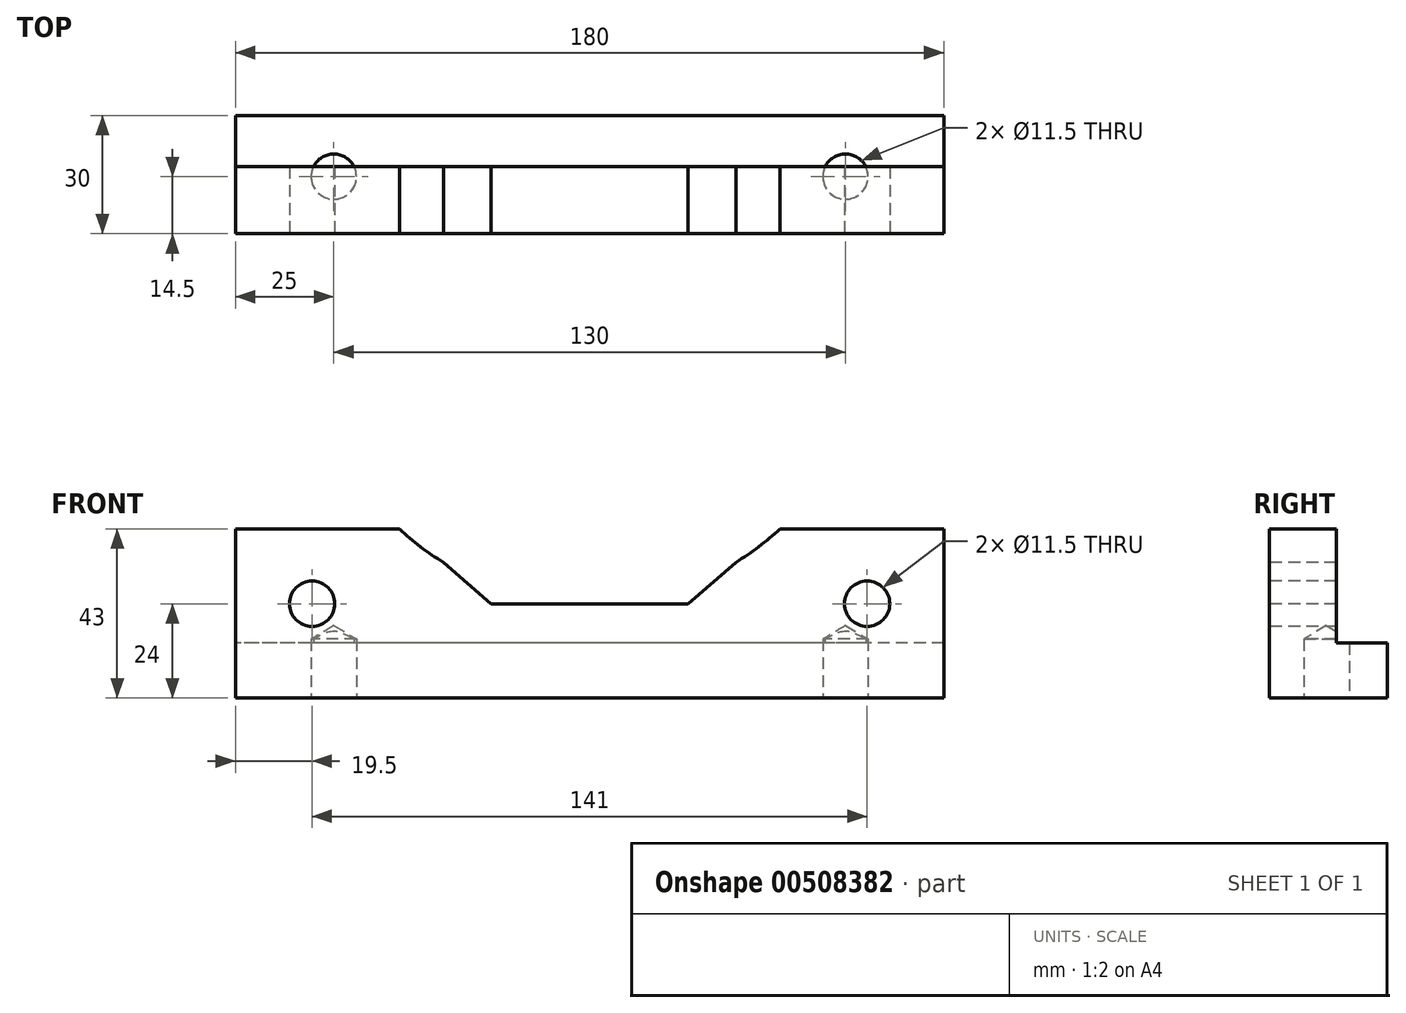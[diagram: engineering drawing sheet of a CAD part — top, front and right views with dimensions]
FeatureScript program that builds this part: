
annotation { "Feature Type Name" : "Feature", "Feature Type Description" : "" }
export const myFeature = defineFeature(function(context is Context, id is Id, definition is map)
    precondition{}
    {
        {
            var Q0;
            Q0=qCreatedBy(makeId("Right.planeOp"),FACE);
            var sketch = newSketch(context, id + "F0", { "sketchPlane" : qUnion([Q0])});
            skLineSegment(sketch, "E0", {"start": v(0, 0) * mm, "end": v(0, 43) * mm});
            skLineSegment(sketch, "E1", {"start": v(0, 43) * mm, "end": v(17, 43) * mm});
            skLineSegment(sketch, "E2", {"start": v(17, 43) * mm, "end": v(17, 14) * mm});
            skLineSegment(sketch, "E3", {"start": v(17, 14) * mm, "end": v(30, 14) * mm});
            skLineSegment(sketch, "E4", {"start": v(30, 14) * mm, "end": v(30, 0) * mm});
            skLineSegment(sketch, "E5", {"start": v(30, 0) * mm, "end": v(0, 0) * mm});
            skSolve(sketch);
        }
        {
            var Q0;
            Q0=makeQuery(id+"F0.imprint","IMPRINT",FACE,{"disambiguationData":[TD([[makeQuery(id+"F0.imprint","IMPRINT",EDGE,{"derivedFrom":sQuery(id+"F0.wireOp",EDGE,"E0")}),-1.0]])]});
            extrude(context, id + "F1", {"entities" : qUnion([Q0]), "endBound" : BoundingType.SYMMETRIC, "depth" : 180 * mm});
        }
        {
            var Q0;
            Q0=makeQuery(id+"F1.opExtrude","SWEPT_FACE",FACE,{"disambiguationData":[OSD([sQuery(id+"F0.wireOp",EDGE,"E5")])]});
            var sketch = newSketch(context, id + "F2", { "sketchPlane" : qUnion([Q0])});
            skLineSegment(sketch, "E6", {"start": v(65, -14.5) * mm, "end": v(-65, -14.5) * mm});
            skLineSegment(sketch, "E7", {"start": v(0, -14.5) * mm, "end": v(0, 0) * mm});
            skSolve(sketch);
        }
        {
            var Q0;
            Q0=sQuery(id+"F2.wireOp",VERTEX,"E6.start");
            var Q1;
            Q1=sQuery(id+"F2.wireOp",VERTEX,"E6.end");
            var Q2;
            Q2=makeQuery(id+"F1.opExtrude","SWEPT_BODY",BODY,{"disambiguationData":[OSD([sQuery(id+"F0.wireOp",EDGE,"E0"),sQuery(id+"F0.wireOp",EDGE,"E1"),sQuery(id+"F0.wireOp",EDGE,"E2"),sQuery(id+"F0.wireOp",EDGE,"E3"),sQuery(id+"F0.wireOp",EDGE,"E4"),sQuery(id+"F0.wireOp",EDGE,"E5")])]});
            hole(context, id + "F3", {"style" : HoleStyle.SIMPLE, "endStyle" : HoleEndStyle.BLIND, "holeDiameter" : 11.5 * mm, "holeDepth" : 15 * mm, "tappedDepth" : 12 * mm, "tapClearance" : 3, "locations" : qUnion([Q0, Q1]), "scope" : qUnion([Q2])});
        }
        {
            var Q0;
            Q0=makeQuery(id+"F1.opExtrude","SWEPT_FACE",FACE,{"disambiguationData":[OSD([sQuery(id+"F0.wireOp",EDGE,"E0")])]});
            var sketch = newSketch(context, id + "F4", { "sketchPlane" : qUnion([Q0])});
            skCircle(sketch, "E8", {"center": v(0, 95) * mm, "radius": 71 * mm});
            skSolve(sketch);
        }
        {
            var Q0;
            {var subQ0=sQuery(id+"F4.wireOp",EDGE,"E8");var subQ1=makeQuery(id+"F1.opExtrude","SWEPT_EDGE",EDGE,{"disambiguationData":[OSD([sQuery(id+"F0.wireOp",EDGE,"E0"),sQuery(id+"F0.wireOp",EDGE,"E1")])]});var subQ2=makeQuery(id+"F4.imprint","INTERSECT",VERTEX,{"disambiguationData":[OD(0.0)],"derivedFrom":[subQ1,subQ0]});Q0=makeQuery(id+"F4.imprint","IMPRINT",FACE,{"disambiguationData":[TD([[makeQuery(id+"F4.imprint","IMPRINT",EDGE,{"disambiguationData":[TD([[subQ2,-1.0]])],"derivedFrom":subQ0}),1.0]])]});}
            extrude(context, id + "F5", {"entities" : qUnion([Q0]), "operationType" : NewBodyOperationType.REMOVE, "endBound" : BoundingType.THROUGH_ALL, "oppositeDirection" : true, "depth" : 25 * mm});
        }
        {
            var Q0;
            Q0=makeQuery(id+"F1.opExtrude","SWEPT_FACE",FACE,{"disambiguationData":[OSD([sQuery(id+"F0.wireOp",EDGE,"E0")])]});
            var sketch = newSketch(context, id + "F6", { "sketchPlane" : qUnion([Q0])});
            skLineSegment(sketch, "E9", {"start": v(70.5, 24) * mm, "end": v(-70.5, 24) * mm});
            skLineSegment(sketch, "E10", {"start": v(0, 24) * mm, "end": v(0, 0) * mm});
            skSolve(sketch);
        }
        {
            var Q0;
            Q0=sQuery(id+"F6.wireOp",VERTEX,"E9.end");
            var Q1;
            Q1=sQuery(id+"F6.wireOp",VERTEX,"E9.start");
            var Q2;
            Q2=makeQuery(id+"F1.opExtrude","SWEPT_BODY",BODY,{"disambiguationData":[OSD([sQuery(id+"F0.wireOp",EDGE,"E0"),sQuery(id+"F0.wireOp",EDGE,"E1"),sQuery(id+"F0.wireOp",EDGE,"E2"),sQuery(id+"F0.wireOp",EDGE,"E3"),sQuery(id+"F0.wireOp",EDGE,"E4"),sQuery(id+"F0.wireOp",EDGE,"E5")])]});
            hole(context, id + "F7", {"style" : HoleStyle.SIMPLE, "endStyle" : HoleEndStyle.THROUGH, "holeDiameter" : 11.5 * mm, "tappedDepth" : 12 * mm, "tapClearance" : 3, "locations" : qUnion([Q0, Q1]), "scope" : qUnion([Q2])});
        }
        {
            var Q0;
            Q0=makeQuery(id+"F1.opExtrude","SWEPT_FACE",FACE,{"disambiguationData":[OSD([sQuery(id+"F0.wireOp",EDGE,"E0")])]});
            var sketch = newSketch(context, id + "F8", { "sketchPlane" : qUnion([Q0])});
            skLineSegment(sketch, "E11", {"start": v(-47, 43) * mm, "end": v(-25, 24) * mm});
            skLineSegment(sketch, "E12", {"start": v(-25, 24) * mm, "end": v(25, 24) * mm});
            skLineSegment(sketch, "E13", {"start": v(25, 24) * mm, "end": v(47, 43) * mm});
            skLineSegment(sketch, "E14", {"start": v(47, 43) * mm, "end": v(-47, 43) * mm});
            skLineSegment(sketch, "E15", {"start": v(0, 43) * mm, "end": v(0, 24) * mm});
            skSolve(sketch);
        }
        {
            var Q0;
            {var subQ0=sQuery(id+"F8.wireOp",EDGE,"E11");Q0=makeQuery(id+"F8.imprint","IMPRINT",FACE,{"disambiguationData":[TD([[makeQuery(id+"F8.imprint","IMPRINT",EDGE,{"derivedFrom":subQ0}),1.0]])]});}
            var Q1;
            {var subQ3=sQuery(id+"F8.wireOp",EDGE,"E15");Q1=makeQuery(id+"F8.imprint","IMPRINT",FACE,{"disambiguationData":[TD([[makeQuery(id+"F8.imprint","IMPRINT",EDGE,{"derivedFrom":subQ3}),1.0]])]});}
            var Q2;
            {var subQ0=sQuery(id+"F8.wireOp",EDGE,"E13");Q2=makeQuery(id+"F8.imprint","IMPRINT",FACE,{"disambiguationData":[TD([[makeQuery(id+"F8.imprint","IMPRINT",EDGE,{"derivedFrom":subQ0}),1.0]])]});}
            extrude(context, id + "F9", {"entities" : qUnion([Q0, Q1, Q2]), "operationType" : NewBodyOperationType.REMOVE, "endBound" : BoundingType.THROUGH_ALL, "oppositeDirection" : true, "depth" : 25 * mm});
        }
    });
